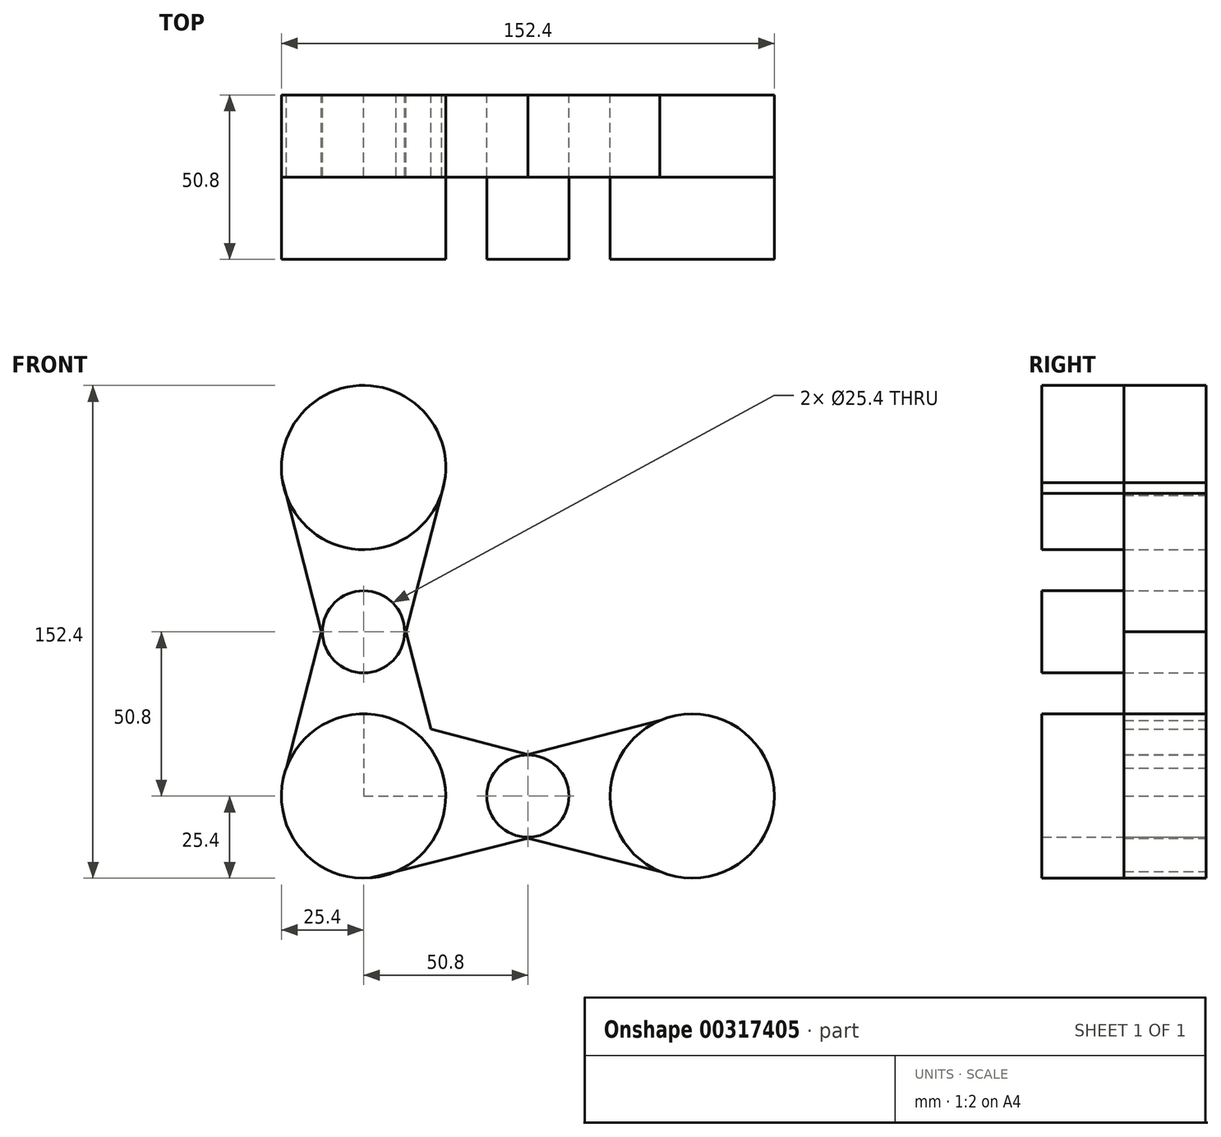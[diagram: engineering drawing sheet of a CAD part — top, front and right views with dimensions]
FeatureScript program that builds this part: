
annotation { "Feature Type Name" : "Feature", "Feature Type Description" : "" }
export const myFeature = defineFeature(function(context is Context, id is Id, definition is map)
    precondition{}
    {
        {
            var Q0;
            Q0=qCreatedBy(makeId("Front.planeOp"),FACE);
            var sketch = newSketch(context, id + "F0", { "sketchPlane" : qUnion([Q0])});
            skLineSegment(sketch, "E0", {"start": v(-50.8, 50.8) * mm, "end": v(-50.8, 0) * mm});
            skLineSegment(sketch, "E1", {"start": v(-50.8, 0) * mm, "end": v(-50.8, -50.8) * mm});
            skLineSegment(sketch, "E2", {"start": v(-50.8, -50.8) * mm, "end": v(0, -50.8) * mm});
            skLineSegment(sketch, "E3", {"start": v(0, -50.8) * mm, "end": v(50.8, -50.8) * mm});
            skCircle(sketch, "E4", {"center": v(-50.8, 50.8) * mm, "radius": 25.4 * mm});
            skCircle(sketch, "E5", {"center": v(-50.8, -50.8) * mm, "radius": 25.4 * mm});
            skCircle(sketch, "E6", {"center": v(50.8, -50.8) * mm, "radius": 25.4 * mm});
            skCircle(sketch, "E7", {"center": v(-50.8, 0) * mm, "radius": 12.7 * mm});
            skCircle(sketch, "E8", {"center": v(0, -50.8) * mm, "radius": 12.7 * mm});
            skLineSegment(sketch, "E9", {"start": v(-75.9, 46.88) * mm, "end": v(-63.9, 0) * mm});
            skLineSegment(sketch, "E10", {"start": v(-63.9, 0) * mm, "end": v(-75.9, -46.88) * mm});
            skLineSegment(sketch, "E11", {"start": v(-25.84, 46.1) * mm, "end": v(-37.69, 0) * mm});
            skLineSegment(sketch, "E12", {"start": v(0, -37.92) * mm, "end": v(48.31, -25.52) * mm});
            skLineSegment(sketch, "E13", {"start": v(-48.58, -76.1) * mm, "end": v(0, -63.9) * mm});
            skLineSegment(sketch, "E14", {"start": v(0, -63.9) * mm, "end": v(48.58, -76.1) * mm});
            skLineSegment(sketch, "E15", {"start": v(-37.69, 0) * mm, "end": v(-25.84, -46.1) * mm});
            skLineSegment(sketch, "E16", {"start": v(0, -37.92) * mm, "end": v(-44.33, -26.24) * mm});
            skSolve(sketch);
        }
        {
            var Q0;
            {var subQ0=sQuery(id+"F0.wireOp",EDGE,"E9");var subQ1=sQuery(id+"F0.wireOp",EDGE,"E4");var subQ2=makeQuery(id+"F0.imprint","INTERSECT",VERTEX,{"disambiguationData":[OD(0.0)],"derivedFrom":[subQ1,subQ0]});Q0=makeQuery(id+"F0.imprint","IMPRINT",FACE,{"disambiguationData":[TD([[makeQuery(id+"F0.imprint","IMPRINT",EDGE,{"disambiguationData":[TD([[subQ2,-1.0]])],"derivedFrom":subQ1}),1.0]])]});}
            var Q1;
            {var subQ0=sQuery(id+"F0.wireOp",EDGE,"E11");var subQ1=sQuery(id+"F0.wireOp",EDGE,"E4");var subQ2=makeQuery(id+"F0.imprint","INTERSECT",VERTEX,{"disambiguationData":[OD(0.0)],"derivedFrom":[subQ1,subQ0]});Q1=makeQuery(id+"F0.imprint","IMPRINT",FACE,{"disambiguationData":[TD([[makeQuery(id+"F0.imprint","IMPRINT",EDGE,{"disambiguationData":[TD([[subQ2,1.0]])],"derivedFrom":subQ1}),1.0]])]});}
            var Q2;
            {var subQ0=sQuery(id+"F0.wireOp",EDGE,"E10");var subQ1=sQuery(id+"F0.wireOp",EDGE,"E5");var subQ2=makeQuery(id+"F0.imprint","INTERSECT",VERTEX,{"disambiguationData":[OD(0.0)],"derivedFrom":[subQ1,subQ0]});Q2=makeQuery(id+"F0.imprint","IMPRINT",FACE,{"disambiguationData":[TD([[makeQuery(id+"F0.imprint","IMPRINT",EDGE,{"disambiguationData":[TD([[subQ2,1.0]])],"derivedFrom":subQ1}),1.0]])]});}
            var Q3;
            {var subQ0=sQuery(id+"F0.wireOp",EDGE,"E13");var subQ1=sQuery(id+"F0.wireOp",EDGE,"E5");var subQ2=makeQuery(id+"F0.imprint","INTERSECT",VERTEX,{"disambiguationData":[OD(0.0)],"derivedFrom":[subQ1,subQ0]});Q3=makeQuery(id+"F0.imprint","IMPRINT",FACE,{"disambiguationData":[TD([[makeQuery(id+"F0.imprint","IMPRINT",EDGE,{"disambiguationData":[TD([[subQ2,-1.0]])],"derivedFrom":subQ1}),1.0]])]});}
            var Q4;
            {var subQ0=sQuery(id+"F0.wireOp",EDGE,"E12");var subQ1=sQuery(id+"F0.wireOp",EDGE,"E6");var subQ2=makeQuery(id+"F0.imprint","INTERSECT",VERTEX,{"disambiguationData":[OD(0.0)],"derivedFrom":[subQ1,subQ0]});Q4=makeQuery(id+"F0.imprint","IMPRINT",FACE,{"disambiguationData":[TD([[makeQuery(id+"F0.imprint","IMPRINT",EDGE,{"disambiguationData":[TD([[subQ2,-1.0]])],"derivedFrom":subQ1}),1.0]])]});}
            var Q5;
            {var subQ0=sQuery(id+"F0.wireOp",EDGE,"E14");var subQ1=sQuery(id+"F0.wireOp",EDGE,"E6");var subQ2=makeQuery(id+"F0.imprint","INTERSECT",VERTEX,{"disambiguationData":[OD(0.0)],"derivedFrom":[subQ1,subQ0]});Q5=makeQuery(id+"F0.imprint","IMPRINT",FACE,{"disambiguationData":[TD([[makeQuery(id+"F0.imprint","IMPRINT",EDGE,{"disambiguationData":[TD([[subQ2,1.0]])],"derivedFrom":subQ1}),1.0]])]});}
            var Q6;
            {var subQ0=sQuery(id+"F0.wireOp",EDGE,"E9");var subQ1=sQuery(id+"F0.wireOp",EDGE,"E4");var subQ2=makeQuery(id+"F0.imprint","INTERSECT",VERTEX,{"disambiguationData":[OD(0.0)],"derivedFrom":[subQ1,subQ0]});Q6=makeQuery(id+"F0.imprint","IMPRINT",FACE,{"disambiguationData":[TD([[makeQuery(id+"F0.imprint","IMPRINT",EDGE,{"disambiguationData":[TD([[subQ2,-1.0]])],"derivedFrom":subQ1}),1.0]])]});}
            var Q7;
            {var subQ0=sQuery(id+"F0.wireOp",EDGE,"E11");var subQ1=sQuery(id+"F0.wireOp",EDGE,"E4");var subQ2=makeQuery(id+"F0.imprint","INTERSECT",VERTEX,{"disambiguationData":[OD(0.0)],"derivedFrom":[subQ1,subQ0]});Q7=makeQuery(id+"F0.imprint","IMPRINT",FACE,{"disambiguationData":[TD([[makeQuery(id+"F0.imprint","IMPRINT",EDGE,{"disambiguationData":[TD([[subQ2,1.0]])],"derivedFrom":subQ1}),1.0]])]});}
            var Q8;
            {var subQ0=sQuery(id+"F0.wireOp",EDGE,"E10");var subQ1=sQuery(id+"F0.wireOp",EDGE,"E5");var subQ2=makeQuery(id+"F0.imprint","INTERSECT",VERTEX,{"disambiguationData":[OD(0.0)],"derivedFrom":[subQ1,subQ0]});Q8=makeQuery(id+"F0.imprint","IMPRINT",FACE,{"disambiguationData":[TD([[makeQuery(id+"F0.imprint","IMPRINT",EDGE,{"disambiguationData":[TD([[subQ2,1.0]])],"derivedFrom":subQ1}),1.0]])]});}
            var Q9;
            {var subQ0=sQuery(id+"F0.wireOp",EDGE,"E13");var subQ1=sQuery(id+"F0.wireOp",EDGE,"E5");var subQ2=makeQuery(id+"F0.imprint","INTERSECT",VERTEX,{"disambiguationData":[OD(0.0)],"derivedFrom":[subQ1,subQ0]});Q9=makeQuery(id+"F0.imprint","IMPRINT",FACE,{"disambiguationData":[TD([[makeQuery(id+"F0.imprint","IMPRINT",EDGE,{"disambiguationData":[TD([[subQ2,-1.0]])],"derivedFrom":subQ1}),1.0]])]});}
            var Q10;
            {var subQ0=sQuery(id+"F0.wireOp",EDGE,"E12");var subQ1=sQuery(id+"F0.wireOp",EDGE,"E6");var subQ2=makeQuery(id+"F0.imprint","INTERSECT",VERTEX,{"disambiguationData":[OD(0.0)],"derivedFrom":[subQ1,subQ0]});Q10=makeQuery(id+"F0.imprint","IMPRINT",FACE,{"disambiguationData":[TD([[makeQuery(id+"F0.imprint","IMPRINT",EDGE,{"disambiguationData":[TD([[subQ2,-1.0]])],"derivedFrom":subQ1}),1.0]])]});}
            var Q11;
            {var subQ0=sQuery(id+"F0.wireOp",EDGE,"E14");var subQ1=sQuery(id+"F0.wireOp",EDGE,"E6");var subQ2=makeQuery(id+"F0.imprint","INTERSECT",VERTEX,{"disambiguationData":[OD(0.0)],"derivedFrom":[subQ1,subQ0]});Q11=makeQuery(id+"F0.imprint","IMPRINT",FACE,{"disambiguationData":[TD([[makeQuery(id+"F0.imprint","IMPRINT",EDGE,{"disambiguationData":[TD([[subQ2,1.0]])],"derivedFrom":subQ1}),1.0]])]});}
            var Q12;
            {var subQ1=sQuery(id+"F0.wireOp",EDGE,"E4");var subQ4=makeQuery(id+"F0.imprint","INTERSECT",VERTEX,{"derivedFrom":[sQuery(id+"F0.wireOp",EDGE,"E0"),subQ1]});Q12=makeQuery(id+"F0.imprint","IMPRINT",FACE,{"disambiguationData":[TD([[makeQuery(id+"F0.imprint","IMPRINT",EDGE,{"disambiguationData":[TD([[subQ4,1.0]])],"derivedFrom":subQ1}),1.0]])]});}
            var Q13;
            {var subQ0=sQuery(id+"F0.wireOp",EDGE,"E1");var subQ1=sQuery(id+"F0.wireOp",EDGE,"E0");var subQ2=makeQuery(id+"F0.imprint","INTERSECT",VERTEX,{"derivedFrom":[subQ1,subQ0]});Q13=makeQuery(id+"F0.imprint","IMPRINT",FACE,{"disambiguationData":[TD([[makeQuery(id+"F0.imprint","IMPRINT",EDGE,{"disambiguationData":[TD([[subQ2,1.0]])],"derivedFrom":subQ1}),-1.0]])]});}
            var Q14;
            {var subQ5=sQuery(id+"F0.wireOp",EDGE,"E2");var subQ6=sQuery(id+"F0.wireOp",EDGE,"E1");var subQ7=makeQuery(id+"F0.imprint","INTERSECT",VERTEX,{"derivedFrom":[subQ6,subQ5]});Q14=makeQuery(id+"F0.imprint","IMPRINT",FACE,{"disambiguationData":[TD([[makeQuery(id+"F0.imprint","IMPRINT",EDGE,{"disambiguationData":[TD([[subQ7,1.0]])],"derivedFrom":subQ6}),-1.0]])]});}
            var Q15;
            {var subQ1=sQuery(id+"F0.wireOp",EDGE,"E6");var subQ5=makeQuery(id+"F0.imprint","INTERSECT",VERTEX,{"derivedFrom":[sQuery(id+"F0.wireOp",EDGE,"E3"),subQ1]});Q15=makeQuery(id+"F0.imprint","IMPRINT",FACE,{"disambiguationData":[TD([[makeQuery(id+"F0.imprint","IMPRINT",EDGE,{"disambiguationData":[TD([[subQ5,1.0]])],"derivedFrom":subQ1}),1.0]])]});}
            var Q16;
            {var subQ0=sQuery(id+"F0.wireOp",EDGE,"E3");var subQ1=sQuery(id+"F0.wireOp",EDGE,"E2");var subQ2=makeQuery(id+"F0.imprint","INTERSECT",VERTEX,{"derivedFrom":[subQ1,subQ0]});Q16=makeQuery(id+"F0.imprint","IMPRINT",FACE,{"disambiguationData":[TD([[makeQuery(id+"F0.imprint","IMPRINT",EDGE,{"disambiguationData":[TD([[subQ2,1.0]])],"derivedFrom":subQ1}),1.0]])]});}
            var Q17;
            {var subQ0=sQuery(id+"F0.wireOp",EDGE,"E3");var subQ1=sQuery(id+"F0.wireOp",EDGE,"E2");var subQ2=makeQuery(id+"F0.imprint","INTERSECT",VERTEX,{"derivedFrom":[subQ1,subQ0]});Q17=makeQuery(id+"F0.imprint","IMPRINT",FACE,{"disambiguationData":[TD([[makeQuery(id+"F0.imprint","IMPRINT",EDGE,{"disambiguationData":[TD([[subQ2,1.0]])],"derivedFrom":subQ1}),-1.0]])]});}
            var Q18;
            {var subQ0=sQuery(id+"F0.wireOp",EDGE,"E1");var subQ1=sQuery(id+"F0.wireOp",EDGE,"E0");var subQ2=makeQuery(id+"F0.imprint","INTERSECT",VERTEX,{"derivedFrom":[subQ1,subQ0]});Q18=makeQuery(id+"F0.imprint","IMPRINT",FACE,{"disambiguationData":[TD([[makeQuery(id+"F0.imprint","IMPRINT",EDGE,{"disambiguationData":[TD([[subQ2,1.0]])],"derivedFrom":subQ1}),1.0]])]});}
            var Q19;
            {var subQ5=sQuery(id+"F0.wireOp",EDGE,"E2");var subQ7=sQuery(id+"F0.wireOp",EDGE,"E1");var subQ8=makeQuery(id+"F0.imprint","INTERSECT",VERTEX,{"derivedFrom":[subQ7,subQ5]});Q19=makeQuery(id+"F0.imprint","IMPRINT",FACE,{"disambiguationData":[TD([[makeQuery(id+"F0.imprint","IMPRINT",EDGE,{"disambiguationData":[TD([[subQ8,1.0]])],"derivedFrom":subQ7}),1.0]])]});}
            extrude(context, id + "F1", {"entities" : qUnion([Q0, Q1, Q2, Q3, Q4, Q5, Q6, Q7, Q8, Q9, Q10, Q11, Q12, Q13, Q14, Q15, Q16, Q17, Q18, Q19]), "depth" : 50.8 * mm});
        }
        {
            var Q0;
            Q0 = qSketchRegion(id + "F0", true);
            extrude(context, id + "F2", {"entities" : qUnion([Q0]), "depth" : 25.4 * mm});
        }
    });
